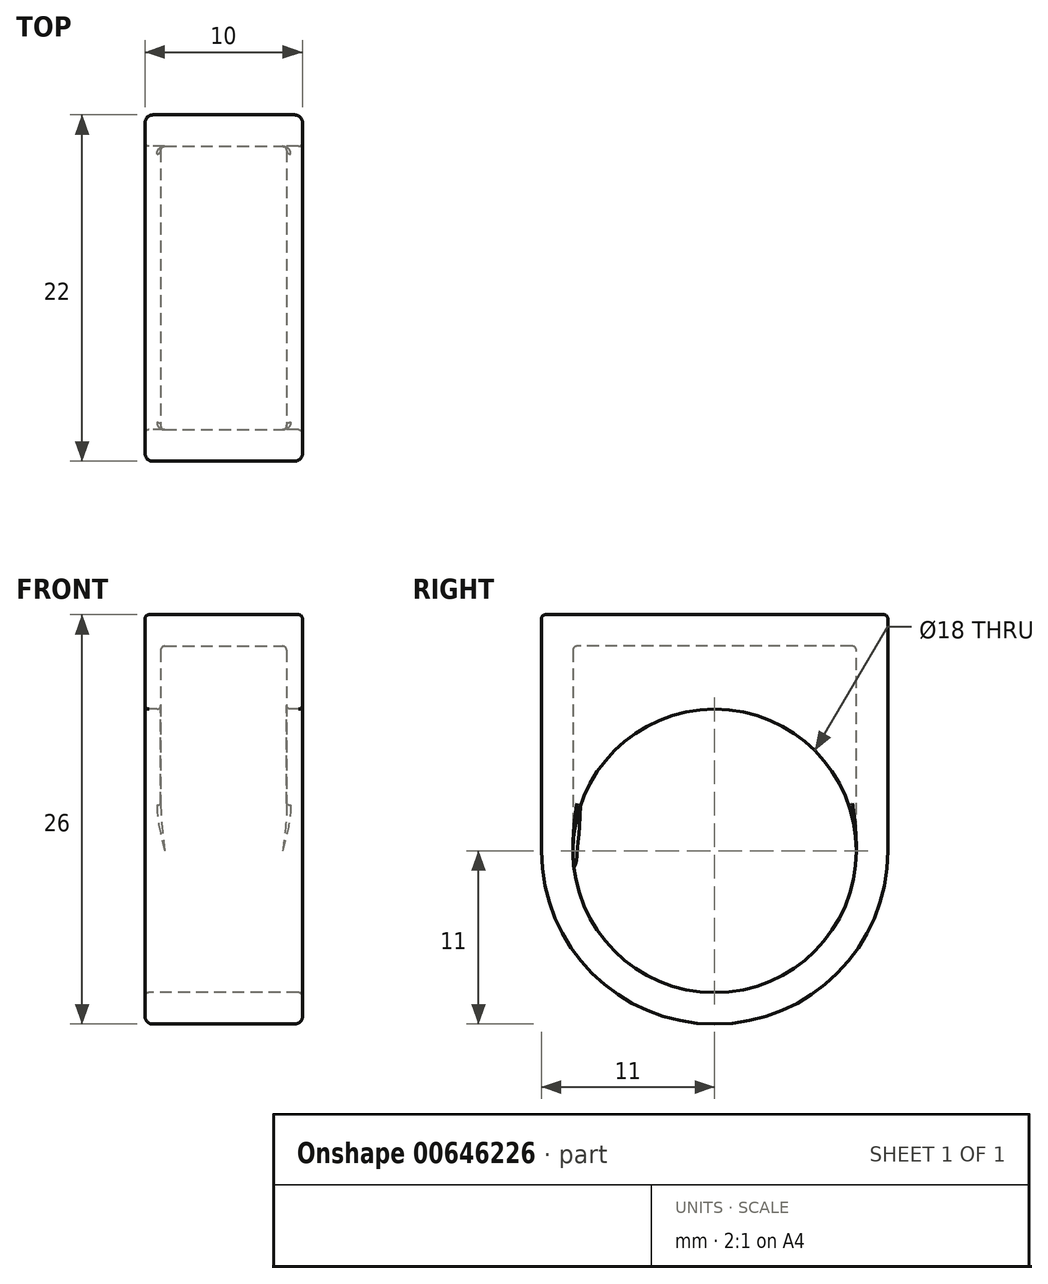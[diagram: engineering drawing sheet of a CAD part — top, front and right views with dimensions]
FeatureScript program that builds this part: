
annotation { "Feature Type Name" : "Feature", "Feature Type Description" : "" }
export const myFeature = defineFeature(function(context is Context, id is Id, definition is map)
    precondition{}
    {
        {
            var Q0;
            Q0=qCreatedBy(makeId("Right.planeOp"),FACE);
            var sketch = newSketch(context, id + "F0", { "sketchPlane" : qUnion([Q0])});
            skCircle(sketch, "E0", {"center": v(0, 0) * mm, "radius": 9 * mm});
            skCircle(sketch, "E1", {"center": v(0, 0) * mm, "radius": 11 * mm});
            skLineSegment(sketch, "E2", {"start": v(-11, 0) * mm, "end": v(-11, 15) * mm});
            skLineSegment(sketch, "E3", {"start": v(11, 0) * mm, "end": v(11, 15) * mm});
            skLineSegment(sketch, "E4", {"start": v(11, 15) * mm, "end": v(-11, 15) * mm});
            skSolve(sketch);
        }
        {
            var Q0;
            Q0 = qSketchRegion(id + "F0", true);
            extrude(context, id + "F1", {"entities" : qUnion([Q0]), "endBound" : BoundingType.SYMMETRIC, "depth" : 10 * mm, "offsetDistance" : 25 * mm});
        }
        {
            var Q0;
            Q0=qCreatedBy(makeId("Right.planeOp"),FACE);
            var sketch = newSketch(context, id + "F2", { "sketchPlane" : qUnion([Q0])});
            skLineSegment(sketch, "E5.0", {"start": v(-9, 13) * mm, "end": v(-9, 0) * mm});
            skLineSegment(sketch, "E5.1", {"start": v(9, 13) * mm, "end": v(-9, 13) * mm});
            skLineSegment(sketch, "E5.2", {"start": v(9, 0) * mm, "end": v(9, 13) * mm});
            skArc(sketch, "E5.3", {"start": v(-9, 0) * mm, "mid": v(0, -9) * mm, "end": v(9, 0) * mm});
            skSolve(sketch);
        }
        {
            var Q0;
            Q0 = qSketchRegion(id + "F2", true);
            extrude(context, id + "F3", {"entities" : qUnion([Q0]), "operationType" : NewBodyOperationType.REMOVE, "endBound" : BoundingType.SYMMETRIC, "oppositeDirection" : true, "depth" : 8 * mm, "offsetDistance" : 25 * mm});
        }
        {
            var Q0;
            Q0=makeQuery(id+"F1.opExtrude","CAP_EDGE",EDGE,{"disambiguationData":[OSD([sQuery(id+"F0.wireOp",EDGE,"E2")])],"isStart":true});
            var Q1;
            Q1=makeQuery(id+"F1.opExtrude","CAP_EDGE",EDGE,{"disambiguationData":[OSD([sQuery(id+"F0.wireOp",EDGE,"E2")])],"isStart":false});
            fillet(context, id + "F4", {"entities" : qUnion([Q0, Q1]), "radius" : .5 * mm, "tangentPropagation" : true, "allowEdgeOverflow" : false});
        }
        {
            var Q0;
            Q0=makeQuery(id+"F1.opExtrude","SWEPT_EDGE",EDGE,{"disambiguationData":[OSD([sQuery(id+"F0.wireOp",EDGE,"E3"),sQuery(id+"F0.wireOp",EDGE,"E4")])]});
            var Q1;
            Q1=makeQuery(id+"F1.opExtrude","CAP_EDGE",EDGE,{"disambiguationData":[OSD([sQuery(id+"F0.wireOp",EDGE,"E0")])],"isStart":true});
            var Q2;
            Q2=makeQuery(id+"F1.opExtrude","CAP_EDGE",EDGE,{"disambiguationData":[OSD([sQuery(id+"F0.wireOp",EDGE,"E0")])],"isStart":false});
            var Q3;
            Q3=makeQuery(id+"F1.opExtrude","SWEPT_EDGE",EDGE,{"disambiguationData":[OSD([sQuery(id+"F0.wireOp",EDGE,"E2"),sQuery(id+"F0.wireOp",EDGE,"E4")])]});
            var Q4;
            Q4=makeQuery(id+"F1.opExtrude","SWEPT_EDGE",EDGE,{"disambiguationData":[OSD([sQuery(id+"F0.wireOp",EDGE,"E1"),sQuery(id+"F0.wireOp",EDGE,"E2")])]});
            var Q5;
            Q5=makeQuery(id+"F3.boolean.opBoolean","COPY",EDGE,{"derivedFrom":makeQuery(id+"F3.opExtrude","SWEPT_EDGE",EDGE,{"disambiguationData":[OSD([sQuery(id+"F2.wireOp",EDGE,"E5.2"),sQuery(id+"F2.wireOp",EDGE,"E5.3")])]})});
            var Q6;
            Q6=makeQuery(id+"F3.boolean.opBoolean","INTERSECT",EDGE,{"derivedFrom":[makeQuery(id+"F1.opExtrude","SWEPT_FACE",FACE,{"disambiguationData":[OSD([sQuery(id+"F0.wireOp",EDGE,"E0")])]}),makeQuery(id+"F3.opExtrude","CAP_FACE",FACE,{"disambiguationData":[OSD([sQuery(id+"F2.wireOp",EDGE,"E5.0"),sQuery(id+"F2.wireOp",EDGE,"E5.1"),sQuery(id+"F2.wireOp",EDGE,"E5.2"),sQuery(id+"F2.wireOp",EDGE,"E5.3")])],"isStart":true})]});
            var Q7;
            {var subQ0=sQuery(id+"F0.wireOp",EDGE,"E1");Q7=makeQuery(id+"F4.opFillet","BLEND_EDGE",EDGE,{"blendedFrom":[makeQuery(id+"F1.opExtrude","CAP_EDGE",EDGE,{"disambiguationData":[OSD([subQ0])],"isStart":true}),makeQuery(id+"F1.opExtrude","SWEPT_FACE",FACE,{"disambiguationData":[OSD([subQ0])]})],"blendedInto":[makeQuery(id+"F1.opExtrude","SWEPT_FACE",FACE,{"disambiguationData":[OSD([subQ0])]})]});}
            var Q8;
            Q8=makeQuery(id+"F4.opFillet","BLEND_EDGE",EDGE,{"blendedFrom":[makeQuery(id+"F1.opExtrude","CAP_EDGE",EDGE,{"disambiguationData":[OSD([sQuery(id+"F0.wireOp",EDGE,"E1")])],"isStart":false}),makeQuery(id+"F1.opExtrude","CAP_EDGE",EDGE,{"disambiguationData":[OSD([sQuery(id+"F0.wireOp",EDGE,"E2")])],"isStart":false})],"blendedInto":[]});
            var Q9;
            {var subQ0=sQuery(id+"F0.wireOp",EDGE,"E1");Q9=makeQuery(id+"F4.opFillet","BLEND_EDGE",EDGE,{"blendedFrom":[makeQuery(id+"F1.opExtrude","CAP_EDGE",EDGE,{"disambiguationData":[OSD([subQ0])],"isStart":false}),makeQuery(id+"F1.opExtrude","CAP_FACE",FACE,{"disambiguationData":[OSD([sQuery(id+"F0.wireOp",EDGE,"E0"),subQ0,sQuery(id+"F0.wireOp",EDGE,"E2"),sQuery(id+"F0.wireOp",EDGE,"E3"),sQuery(id+"F0.wireOp",EDGE,"E4")])],"isStart":false})],"blendedInto":[makeQuery(id+"F1.opExtrude","CAP_FACE",FACE,{"disambiguationData":[OSD([sQuery(id+"F0.wireOp",EDGE,"E0"),subQ0,sQuery(id+"F0.wireOp",EDGE,"E2"),sQuery(id+"F0.wireOp",EDGE,"E3"),sQuery(id+"F0.wireOp",EDGE,"E4")])],"isStart":false})]});}
            var Q10;
            {var subQ0=sQuery(id+"F0.wireOp",EDGE,"E1");Q10=makeQuery(id+"F4.opFillet","BLEND_EDGE",EDGE,{"blendedFrom":[makeQuery(id+"F1.opExtrude","CAP_EDGE",EDGE,{"disambiguationData":[OSD([subQ0])],"isStart":false}),makeQuery(id+"F1.opExtrude","SWEPT_FACE",FACE,{"disambiguationData":[OSD([subQ0])]})],"blendedInto":[makeQuery(id+"F1.opExtrude","SWEPT_FACE",FACE,{"disambiguationData":[OSD([subQ0])]})]});}
            var Q11;
            Q11=makeQuery(id+"F4.opFillet","BLEND_EDGE",EDGE,{"blendedFrom":[makeQuery(id+"F1.opExtrude","CAP_EDGE",EDGE,{"disambiguationData":[OSD([sQuery(id+"F0.wireOp",EDGE,"E2")])],"isStart":false}),makeQuery(id+"F1.opExtrude","SWEPT_FACE",FACE,{"disambiguationData":[OSD([sQuery(id+"F0.wireOp",EDGE,"E4")])]})],"blendedInto":[makeQuery(id+"F1.opExtrude","SWEPT_FACE",FACE,{"disambiguationData":[OSD([sQuery(id+"F0.wireOp",EDGE,"E4")])]})]});
            var Q12;
            Q12=makeQuery(id+"F1.opExtrude","CAP_EDGE",EDGE,{"disambiguationData":[OSD([sQuery(id+"F0.wireOp",EDGE,"E4")])],"isStart":true});
            var Q13;
            Q13=makeQuery(id+"F1.opExtrude","CAP_EDGE",EDGE,{"disambiguationData":[OSD([sQuery(id+"F0.wireOp",EDGE,"E4")])],"isStart":false});
            var Q14;
            {var subQ0=sQuery(id+"F0.wireOp",EDGE,"E1");Q14=makeQuery(id+"F4.opFillet","BLEND_EDGE",EDGE,{"blendedFrom":[makeQuery(id+"F1.opExtrude","CAP_EDGE",EDGE,{"disambiguationData":[OSD([subQ0])],"isStart":true}),makeQuery(id+"F1.opExtrude","CAP_FACE",FACE,{"disambiguationData":[OSD([sQuery(id+"F0.wireOp",EDGE,"E0"),subQ0,sQuery(id+"F0.wireOp",EDGE,"E2"),sQuery(id+"F0.wireOp",EDGE,"E3"),sQuery(id+"F0.wireOp",EDGE,"E4")])],"isStart":true})],"blendedInto":[makeQuery(id+"F1.opExtrude","CAP_FACE",FACE,{"disambiguationData":[OSD([sQuery(id+"F0.wireOp",EDGE,"E0"),subQ0,sQuery(id+"F0.wireOp",EDGE,"E2"),sQuery(id+"F0.wireOp",EDGE,"E3"),sQuery(id+"F0.wireOp",EDGE,"E4")])],"isStart":true})]});}
            var Q15;
            Q15=makeQuery(id+"F4.opFillet","BLEND_EDGE",EDGE,{"blendedFrom":[makeQuery(id+"F1.opExtrude","CAP_EDGE",EDGE,{"disambiguationData":[OSD([sQuery(id+"F0.wireOp",EDGE,"E1")])],"isStart":true}),makeQuery(id+"F1.opExtrude","CAP_EDGE",EDGE,{"disambiguationData":[OSD([sQuery(id+"F0.wireOp",EDGE,"E2")])],"isStart":true})],"blendedInto":[]});
            var Q16;
            Q16=makeQuery(id+"F1.opExtrude","SWEPT_EDGE",EDGE,{"disambiguationData":[OSD([sQuery(id+"F0.wireOp",EDGE,"E1"),sQuery(id+"F0.wireOp",EDGE,"E3")])]});
            var Q17;
            {var subQ0=sQuery(id+"F0.wireOp",EDGE,"E2");Q17=makeQuery(id+"F4.opFillet","BLEND_EDGE",EDGE,{"blendedFrom":[makeQuery(id+"F1.opExtrude","CAP_EDGE",EDGE,{"disambiguationData":[OSD([subQ0])],"isStart":false}),makeQuery(id+"F1.opExtrude","CAP_FACE",FACE,{"disambiguationData":[OSD([sQuery(id+"F0.wireOp",EDGE,"E0"),sQuery(id+"F0.wireOp",EDGE,"E1"),subQ0,sQuery(id+"F0.wireOp",EDGE,"E3"),sQuery(id+"F0.wireOp",EDGE,"E4")])],"isStart":false})],"blendedInto":[makeQuery(id+"F1.opExtrude","CAP_FACE",FACE,{"disambiguationData":[OSD([sQuery(id+"F0.wireOp",EDGE,"E0"),sQuery(id+"F0.wireOp",EDGE,"E1"),subQ0,sQuery(id+"F0.wireOp",EDGE,"E3"),sQuery(id+"F0.wireOp",EDGE,"E4")])],"isStart":false})]});}
            var Q18;
            Q18=makeQuery(id+"F4.opFillet","BLEND_EDGE",EDGE,{"blendedFrom":[makeQuery(id+"F1.opExtrude","CAP_EDGE",EDGE,{"disambiguationData":[OSD([sQuery(id+"F0.wireOp",EDGE,"E2")])],"isStart":true}),makeQuery(id+"F1.opExtrude","SWEPT_FACE",FACE,{"disambiguationData":[OSD([sQuery(id+"F0.wireOp",EDGE,"E4")])]})],"blendedInto":[makeQuery(id+"F1.opExtrude","SWEPT_FACE",FACE,{"disambiguationData":[OSD([sQuery(id+"F0.wireOp",EDGE,"E4")])]})]});
            var Q19;
            {var subQ0=sQuery(id+"F0.wireOp",EDGE,"E2");Q19=makeQuery(id+"F4.opFillet","BLEND_EDGE",EDGE,{"blendedFrom":[makeQuery(id+"F1.opExtrude","CAP_EDGE",EDGE,{"disambiguationData":[OSD([subQ0])],"isStart":true}),makeQuery(id+"F1.opExtrude","SWEPT_FACE",FACE,{"disambiguationData":[OSD([subQ0])]})],"blendedInto":[makeQuery(id+"F1.opExtrude","SWEPT_FACE",FACE,{"disambiguationData":[OSD([subQ0])]})]});}
            var Q20;
            Q20=makeQuery(id+"F3.boolean.opBoolean","COPY",EDGE,{"derivedFrom":makeQuery(id+"F3.opExtrude","SWEPT_EDGE",EDGE,{"disambiguationData":[OSD([sQuery(id+"F2.wireOp",EDGE,"E5.0"),sQuery(id+"F2.wireOp",EDGE,"E5.1")])]})});
            var Q21;
            Q21=makeQuery(id+"F3.boolean.opBoolean","COPY",EDGE,{"derivedFrom":makeQuery(id+"F3.opExtrude","SWEPT_EDGE",EDGE,{"disambiguationData":[OSD([sQuery(id+"F2.wireOp",EDGE,"E5.0"),sQuery(id+"F2.wireOp",EDGE,"E5.3")])]})});
            var Q22;
            Q22=makeQuery(id+"F3.boolean.opBoolean","COPY",EDGE,{"derivedFrom":makeQuery(id+"F3.opExtrude","SWEPT_EDGE",EDGE,{"disambiguationData":[OSD([sQuery(id+"F2.wireOp",EDGE,"E5.1"),sQuery(id+"F2.wireOp",EDGE,"E5.2")])]})});
            var Q23;
            Q23=makeQuery(id+"F3.boolean.opBoolean","COPY",EDGE,{"derivedFrom":makeQuery(id+"F3.opExtrude","CAP_EDGE",EDGE,{"disambiguationData":[OSD([sQuery(id+"F2.wireOp",EDGE,"E5.1")])],"isStart":true})});
            var Q24;
            Q24=makeQuery(id+"F3.boolean.opBoolean","COPY",EDGE,{"derivedFrom":makeQuery(id+"F3.opExtrude","CAP_EDGE",EDGE,{"disambiguationData":[OSD([sQuery(id+"F2.wireOp",EDGE,"E5.1")])],"isStart":false})});
            var Q25;
            Q25=makeQuery(id+"F3.boolean.opBoolean","COPY",EDGE,{"derivedFrom":makeQuery(id+"F3.opExtrude","CAP_EDGE",EDGE,{"disambiguationData":[OSD([sQuery(id+"F2.wireOp",EDGE,"E5.2")])],"isStart":true})});
            var Q26;
            Q26=makeQuery(id+"F3.boolean.opBoolean","COPY",EDGE,{"derivedFrom":makeQuery(id+"F3.opExtrude","CAP_EDGE",EDGE,{"disambiguationData":[OSD([sQuery(id+"F2.wireOp",EDGE,"E5.2")])],"isStart":false})});
            var Q27;
            Q27=makeQuery(id+"F3.boolean.opBoolean","INTERSECT",EDGE,{"derivedFrom":[makeQuery(id+"F1.opExtrude","SWEPT_FACE",FACE,{"disambiguationData":[OSD([sQuery(id+"F0.wireOp",EDGE,"E0")])]}),makeQuery(id+"F3.opExtrude","CAP_FACE",FACE,{"disambiguationData":[OSD([sQuery(id+"F2.wireOp",EDGE,"E5.0"),sQuery(id+"F2.wireOp",EDGE,"E5.1"),sQuery(id+"F2.wireOp",EDGE,"E5.2"),sQuery(id+"F2.wireOp",EDGE,"E5.3")])],"isStart":false})]});
            var Q28;
            Q28=makeQuery(id+"F4.opFillet","BLEND_EDGE",EDGE,{"blendedFrom":[makeQuery(id+"F1.opExtrude","CAP_EDGE",EDGE,{"disambiguationData":[OSD([sQuery(id+"F0.wireOp",EDGE,"E1")])],"isStart":false}),makeQuery(id+"F1.opExtrude","CAP_EDGE",EDGE,{"disambiguationData":[OSD([sQuery(id+"F0.wireOp",EDGE,"E3")])],"isStart":false})],"blendedInto":[]});
            var Q29;
            {var subQ0=sQuery(id+"F0.wireOp",EDGE,"E2");Q29=makeQuery(id+"F4.opFillet","BLEND_EDGE",EDGE,{"blendedFrom":[makeQuery(id+"F1.opExtrude","CAP_EDGE",EDGE,{"disambiguationData":[OSD([subQ0])],"isStart":false}),makeQuery(id+"F1.opExtrude","SWEPT_FACE",FACE,{"disambiguationData":[OSD([subQ0])]})],"blendedInto":[makeQuery(id+"F1.opExtrude","SWEPT_FACE",FACE,{"disambiguationData":[OSD([subQ0])]})]});}
            var Q30;
            {var subQ0=sQuery(id+"F0.wireOp",EDGE,"E3");Q30=makeQuery(id+"F4.opFillet","BLEND_EDGE",EDGE,{"blendedFrom":[makeQuery(id+"F1.opExtrude","CAP_EDGE",EDGE,{"disambiguationData":[OSD([subQ0])],"isStart":true}),makeQuery(id+"F1.opExtrude","CAP_FACE",FACE,{"disambiguationData":[OSD([sQuery(id+"F0.wireOp",EDGE,"E0"),sQuery(id+"F0.wireOp",EDGE,"E1"),sQuery(id+"F0.wireOp",EDGE,"E2"),subQ0,sQuery(id+"F0.wireOp",EDGE,"E4")])],"isStart":true})],"blendedInto":[makeQuery(id+"F1.opExtrude","CAP_FACE",FACE,{"disambiguationData":[OSD([sQuery(id+"F0.wireOp",EDGE,"E0"),sQuery(id+"F0.wireOp",EDGE,"E1"),sQuery(id+"F0.wireOp",EDGE,"E2"),subQ0,sQuery(id+"F0.wireOp",EDGE,"E4")])],"isStart":true})]});}
            var Q31;
            {var subQ0=sQuery(id+"F0.wireOp",EDGE,"E3");Q31=makeQuery(id+"F4.opFillet","BLEND_EDGE",EDGE,{"blendedFrom":[makeQuery(id+"F1.opExtrude","CAP_EDGE",EDGE,{"disambiguationData":[OSD([subQ0])],"isStart":true}),makeQuery(id+"F1.opExtrude","SWEPT_FACE",FACE,{"disambiguationData":[OSD([subQ0])]})],"blendedInto":[makeQuery(id+"F1.opExtrude","SWEPT_FACE",FACE,{"disambiguationData":[OSD([subQ0])]})]});}
            var Q32;
            Q32=makeQuery(id+"F4.opFillet","BLEND_EDGE",EDGE,{"blendedFrom":[makeQuery(id+"F1.opExtrude","CAP_EDGE",EDGE,{"disambiguationData":[OSD([sQuery(id+"F0.wireOp",EDGE,"E3")])],"isStart":true}),makeQuery(id+"F1.opExtrude","SWEPT_FACE",FACE,{"disambiguationData":[OSD([sQuery(id+"F0.wireOp",EDGE,"E4")])]})],"blendedInto":[makeQuery(id+"F1.opExtrude","SWEPT_FACE",FACE,{"disambiguationData":[OSD([sQuery(id+"F0.wireOp",EDGE,"E4")])]})]});
            var Q33;
            {var subQ0=sQuery(id+"F0.wireOp",EDGE,"E3");Q33=makeQuery(id+"F4.opFillet","BLEND_EDGE",EDGE,{"blendedFrom":[makeQuery(id+"F1.opExtrude","CAP_EDGE",EDGE,{"disambiguationData":[OSD([subQ0])],"isStart":false}),makeQuery(id+"F1.opExtrude","CAP_FACE",FACE,{"disambiguationData":[OSD([sQuery(id+"F0.wireOp",EDGE,"E0"),sQuery(id+"F0.wireOp",EDGE,"E1"),sQuery(id+"F0.wireOp",EDGE,"E2"),subQ0,sQuery(id+"F0.wireOp",EDGE,"E4")])],"isStart":false})],"blendedInto":[makeQuery(id+"F1.opExtrude","CAP_FACE",FACE,{"disambiguationData":[OSD([sQuery(id+"F0.wireOp",EDGE,"E0"),sQuery(id+"F0.wireOp",EDGE,"E1"),sQuery(id+"F0.wireOp",EDGE,"E2"),subQ0,sQuery(id+"F0.wireOp",EDGE,"E4")])],"isStart":false})]});}
            var Q34;
            Q34=makeQuery(id+"F4.opFillet","BLEND_EDGE",EDGE,{"blendedFrom":[makeQuery(id+"F1.opExtrude","CAP_EDGE",EDGE,{"disambiguationData":[OSD([sQuery(id+"F0.wireOp",EDGE,"E3")])],"isStart":false}),makeQuery(id+"F1.opExtrude","SWEPT_FACE",FACE,{"disambiguationData":[OSD([sQuery(id+"F0.wireOp",EDGE,"E4")])]})],"blendedInto":[makeQuery(id+"F1.opExtrude","SWEPT_FACE",FACE,{"disambiguationData":[OSD([sQuery(id+"F0.wireOp",EDGE,"E4")])]})]});
            var Q35;
            Q35=makeQuery(id+"F4.opFillet","BLEND_EDGE",EDGE,{"blendedFrom":[makeQuery(id+"F1.opExtrude","CAP_EDGE",EDGE,{"disambiguationData":[OSD([sQuery(id+"F0.wireOp",EDGE,"E1")])],"isStart":true}),makeQuery(id+"F1.opExtrude","CAP_EDGE",EDGE,{"disambiguationData":[OSD([sQuery(id+"F0.wireOp",EDGE,"E3")])],"isStart":true})],"blendedInto":[]});
            var Q36;
            Q36=makeQuery(id+"F3.boolean.opBoolean","COPY",EDGE,{"derivedFrom":makeQuery(id+"F3.opExtrude","CAP_EDGE",EDGE,{"disambiguationData":[OSD([sQuery(id+"F2.wireOp",EDGE,"E5.0")])],"isStart":true})});
            var Q37;
            Q37=makeQuery(id+"F3.boolean.opBoolean","COPY",EDGE,{"derivedFrom":makeQuery(id+"F3.opExtrude","CAP_EDGE",EDGE,{"disambiguationData":[OSD([sQuery(id+"F2.wireOp",EDGE,"E5.0")])],"isStart":false})});
            var Q38;
            {var subQ0=sQuery(id+"F0.wireOp",EDGE,"E2");Q38=makeQuery(id+"F4.opFillet","BLEND_EDGE",EDGE,{"blendedFrom":[makeQuery(id+"F1.opExtrude","CAP_EDGE",EDGE,{"disambiguationData":[OSD([subQ0])],"isStart":true}),makeQuery(id+"F1.opExtrude","CAP_FACE",FACE,{"disambiguationData":[OSD([sQuery(id+"F0.wireOp",EDGE,"E0"),sQuery(id+"F0.wireOp",EDGE,"E1"),subQ0,sQuery(id+"F0.wireOp",EDGE,"E3"),sQuery(id+"F0.wireOp",EDGE,"E4")])],"isStart":true})],"blendedInto":[makeQuery(id+"F1.opExtrude","CAP_FACE",FACE,{"disambiguationData":[OSD([sQuery(id+"F0.wireOp",EDGE,"E0"),sQuery(id+"F0.wireOp",EDGE,"E1"),subQ0,sQuery(id+"F0.wireOp",EDGE,"E3"),sQuery(id+"F0.wireOp",EDGE,"E4")])],"isStart":true})]});}
            var Q39;
            {var subQ0=sQuery(id+"F0.wireOp",EDGE,"E3");Q39=makeQuery(id+"F4.opFillet","BLEND_EDGE",EDGE,{"blendedFrom":[makeQuery(id+"F1.opExtrude","CAP_EDGE",EDGE,{"disambiguationData":[OSD([subQ0])],"isStart":false}),makeQuery(id+"F1.opExtrude","SWEPT_FACE",FACE,{"disambiguationData":[OSD([subQ0])]})],"blendedInto":[makeQuery(id+"F1.opExtrude","SWEPT_FACE",FACE,{"disambiguationData":[OSD([subQ0])]})]});}
            fillet(context, id + "F5", {"entities" : qUnion([Q0, Q1, Q2, Q3, Q4, Q5, Q6, Q7, Q8, Q9, Q10, Q11, Q12, Q13, Q14, Q15, Q16, Q17, Q18, Q19, Q20, Q21, Q22, Q23, Q24, Q25, Q26, Q27, Q28, Q29, Q30, Q31, Q32, Q33, Q34, Q35, Q36, Q37, Q38, Q39]), "radius" : .25 * mm, "tangentPropagation" : true, "allowEdgeOverflow" : false});
        }
    });
